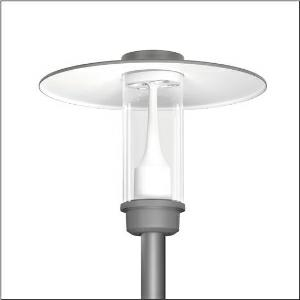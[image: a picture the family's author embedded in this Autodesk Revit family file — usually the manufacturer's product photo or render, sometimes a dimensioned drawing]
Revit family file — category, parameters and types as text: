
# Revit family: litepole_2_iq___st1_2a_5xa5425mf14hp_68c7
name_source: partatom
category: Lighting Fixtures
units: mm (PartAtom-declared; Revit-internal decimal feet)

## family parameters
Cut with Voids When Loaded = No
Host = Face
Light Source = No
Part Type = Normal
Room Calculation Point = No
Round Connector Dimension = Use Diameter
Shared = No

## types (1)
- --- (1 x LED, 4270 lm, 33.6 W, 2700K)
    Apparent Load = 34 VA
    CIE Flux Codes = 22 59 92 98 100
    Color Rendering = 70
    Color Temperature = 2700K
    Default Elevation = 1800 mm
    Description = Litepole 2 iQ, mast luminaire, Module 540 iQ-SR, primary light control with 3 zone facetted reflector, of plastic, silver coated, highly specular, structured, primary optical cover: cover, of PMMA, transparent, light distribution: ST1.2a, light emission: direct distribution, primary light characteristic: asymmetric, installation type: post-top, LED, High Power LED, rated luminous flux: 4.270lm, luminous efficacy: 127lm/W, light colour: 727, colour temperature: 2700K, control gear: iQ Street-Remote, control: pre-setting: logarithmic dimming characteristic, Street-Remote, Auto-Match, Temp-Guard, Lumen-Switch, Night-Set, Smart-Wire, Light-Fading, Desk-Remote (wireless, voltage-free reading and setting of iQ features in the workshop via application-optimized NFC function/RFID function), optimised constant luminous flux control (CLO 2.0), with terminal, 6-pole, max. 2.5mm², mains connection: 230..240V, AC, 50/60Hz, start of lifetime: 34W, end of service life: 36W, reduction: 15W, luminaire housing, upper part, of aluminium, coated, Siteco® metallic grey (DB 702S), diameter: 750mm, height: 590mm, spigot size: d x l = 76 x 70mm (post-top) | with reducer (optional accessory) 60 x 70mm, mounting height: 3..5m, post-top mast mounting element, of diecast aluminium, coated, Siteco® metallic grey (DB 702S), Module 540 iQ-SR, traffic white (RAL 9016), equipment: Power, protection rating (complete): IP65, insulation class (complete): insulation class II (safety insulation), certification: CE, ENEC, VDE, packaging unit: 1 piece

Light Distribution: ST1.2a
    Height = 590 mm
    Lamp = 1 x LED
    Lamp Light Flux = 4270 lm
    Lamp Power = 33.6 W
    Lamp count = 1
    Length = 750 mm
    Luminous efficacy = 127 lm/W
    Manufacturer = Siteco
    ModVariant = No
    Model = 5XA5425MF14HP
    Number of Poles = 1
    OnlyDefault = Yes
    Power Factor = 1
    Product Name = Litepole 2 iQ | ST1.2a
    Product group = mast luminaire | pylon top
    ProductGroupID = 6100
    Protection Class = Protection class II
    Protection Degree = IP 65
    RLX_Detail_Level = 1
    RLX_Emergency_Light_Flux = 0 lm
    RLX_Emergency_Type = 0
    RLX_Emergency_Type_DB = No
    RlxData = <blob elided: 31977 chars, md5=71c8090d>
    Socket = socket
    Standby Power = 0 W
    System Light Flux = 4270 lm
    System Power = 34 W
    Type Comments = factory setting: luminous flux: 100 % | dim-lin: 254 | 695 mA
    Type Image = l_1006518.jpg
    URL = http://relux.com
    VarID = @adj_151817
    Voltage = 0 V
    Weight = 0.00 kg
    Width = 0 mm  [stored 0 ft]

note: [stored X ft] marks values corroborated as IEEE doubles in the binary element streams (Revit-internal decimal feet)

## geometry (parser evidence)
native form markers: Blend x4, Sweep x9
no freeform markers — native parametric forms only
